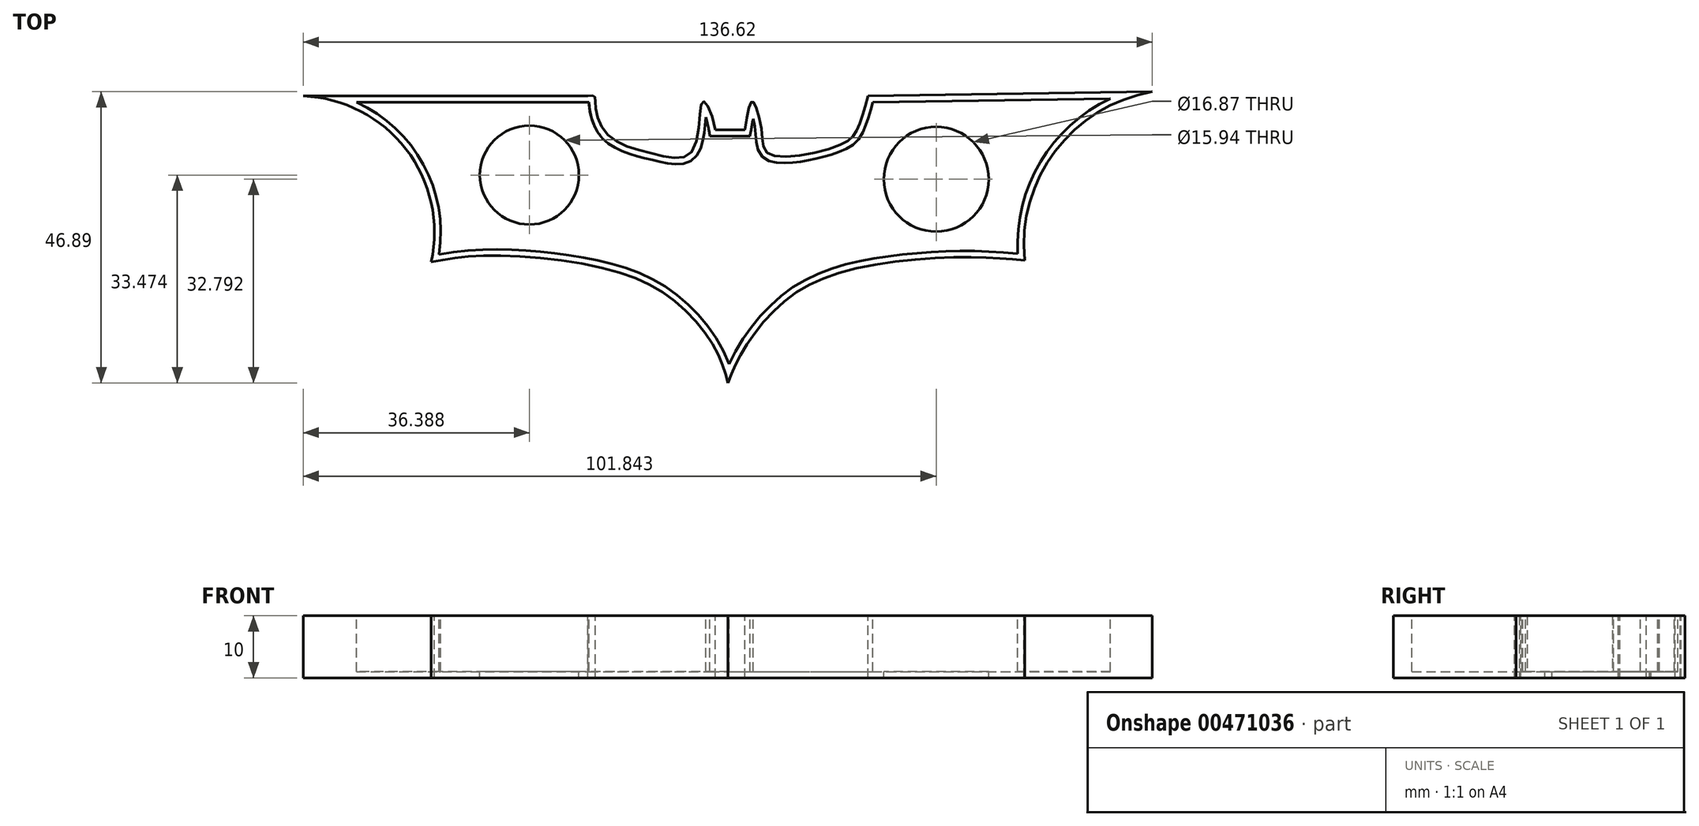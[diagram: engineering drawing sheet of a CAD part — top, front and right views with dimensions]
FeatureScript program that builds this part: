
annotation { "Feature Type Name" : "Feature", "Feature Type Description" : "" }
export const myFeature = defineFeature(function(context is Context, id is Id, definition is map)
    precondition{}
    {
        {
            var Q0;
            Q0=qCreatedBy(makeId("Top.planeOp"),FACE);
            var sketch = newSketch(context, id + "F0", { "sketchPlane" : qUnion([Q0])});
            skArc(sketch, "E0", {"start": v(-47.73, 16.11) * mm, "mid": v(-51.78, 34.28) * mm, "end": v(-68.32, 42.82) * mm});
            skArc(sketch, "E1", {"start": v(68.3, 43.53) * mm, "mid": v(52.68, 33.98) * mm, "end": v(47.74, 16.36) * mm});
            skLineSegment(sketch, "E2", {"start": v(-68.32, 42.82) * mm, "end": v(-22.55, 42.82) * mm});
            skLineSegment(sketch, "E3", {"start": v(22.53, 42.82) * mm, "end": v(68.3, 43.53) * mm});
            skLineSegment(sketch, "E4", {"start": v(-2.04, 37.36) * mm, "end": v(2.72, 37.36) * mm});
            skFitSpline(sketch, "E5", {"points": [v(-22.55, 42.82) * mm, v(-21.5, 42.82) * mm, v(-21.35, 41.77) * mm, v(-19.57, 36.84) * mm, v(-11.89, 33.5) * mm, v(-5.69, 34.03) * mm, v(-4.1, 41.89) * mm, v(-2.04, 37.36) * mm], "startDerivative": vector(18.6, 3) * mm, "endDerivative": vector(8.12, -53.92) * mm});
            skFitSpline(sketch, "E6", {"points": [v(2.72, 37.36) * mm, v(3.95, 41.97) * mm, v(5.42, 37.36) * mm, v(6.76, 33.42) * mm, v(18.04, 34.95) * mm, v(20.78, 37.36) * mm, v(22.53, 42.82) * mm], "startDerivative": vector(9.23, 47.77) * mm, "endDerivative": vector(9.76, 38) * mm});
            skFitSpline(sketch, "E7", {"points": [v(0, -3.36) * mm, v(2.3, 1.58) * mm, v(8.55, 9.31) * mm, v(19.5, 14.82) * mm, v(38.25, 16.88) * mm, v(47.74, 16.36) * mm], "startDerivative": vector(13.14, 32.83) * mm, "endDerivative": vector(44.84, -4.28) * mm});
            skFitSpline(sketch, "E8", {"points": [v(0, -3.36) * mm, v(-1.65, 1.41) * mm, v(-7.74, 9.15) * mm, v(-18.85, 14.82) * mm, v(-38.76, 17.13) * mm, v(-47.73, 16.11) * mm], "startDerivative": vector(-8.33, 32.95) * mm, "endDerivative": vector(-42.52, -7.74) * mm});
            skSolve(sketch);
        }
        {
            var Q0;
            Q0 = qSketchRegion(id + "F0", true);
            extrude(context, id + "F1", {"entities" : qUnion([Q0]), "oppositeDirection" : true, "depth" : 10 * mm});
        }
        {
            var Q0;
            Q0=makeQuery(id+"F1.opExtrude","CAP_FACE",FACE,{"disambiguationData":[OSD([sQuery(id+"F0.wireOp",EDGE,"E0"),sQuery(id+"F0.wireOp",EDGE,"E1"),sQuery(id+"F0.wireOp",EDGE,"E2"),sQuery(id+"F0.wireOp",EDGE,"E3"),sQuery(id+"F0.wireOp",EDGE,"E4"),sQuery(id+"F0.wireOp",EDGE,"E5"),sQuery(id+"F0.wireOp",EDGE,"E6"),sQuery(id+"F0.wireOp",EDGE,"E7"),sQuery(id+"F0.wireOp",EDGE,"E8")])],"isStart":true});
            shell(context, id + "F2", {"entities" : qUnion([Q0]), "thickness" : 1 * mm});
        }
        {
            var Q0;
            Q0=makeQuery(id+"F2.opShell","OFFSET_FACE",FACE,{"disambiguationData":[OSD([sQuery(id+"F0.wireOp",EDGE,"E0"),sQuery(id+"F0.wireOp",EDGE,"E1"),sQuery(id+"F0.wireOp",EDGE,"E2"),sQuery(id+"F0.wireOp",EDGE,"E3"),sQuery(id+"F0.wireOp",EDGE,"E4"),sQuery(id+"F0.wireOp",EDGE,"E5"),sQuery(id+"F0.wireOp",EDGE,"E6"),sQuery(id+"F0.wireOp",EDGE,"E7"),sQuery(id+"F0.wireOp",EDGE,"E8")])]});
            var sketch = newSketch(context, id + "F3", { "sketchPlane" : qUnion([Q0])});
            skCircle(sketch, "E9", {"center": v(-31.93, 30.11) * mm, "radius": 7.97 * mm});
            skCircle(sketch, "E10", {"center": v(33.52, 29.43) * mm, "radius": 8.44 * mm});
            skSolve(sketch);
        }
        {
            var Q0;
            Q0 = qSketchRegion(id + "F3", true);
            extrude(context, id + "F4", {"entities" : qUnion([Q0]), "operationType" : NewBodyOperationType.REMOVE, "oppositeDirection" : true, "depth" : 25 * mm});
        }
    });
